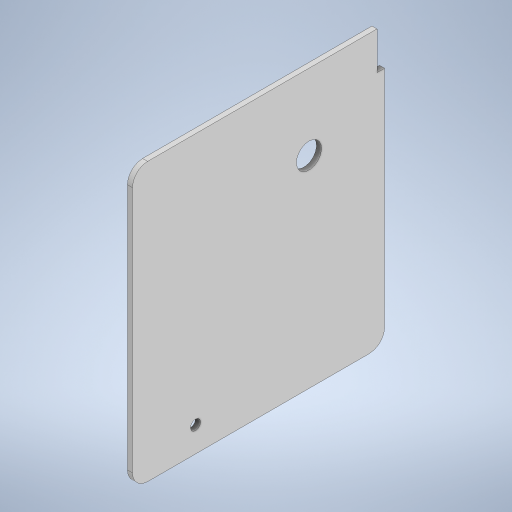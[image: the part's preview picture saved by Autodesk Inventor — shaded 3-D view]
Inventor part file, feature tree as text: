
AUTODESK INVENTOR PART (.ipt)
format: ipt  version: 2024.3 (Build 283343000, 343)  size: 229,376 bytes
history: native  units: mm
features: sheet_metal_op x1, chamfer x1, sketch x1, other x1
ambient origin geometry x8: Origin, YZ Plane, XZ Plane, XY Plane, X Axis, Y Axis, Z Axis, Center Point
bodies: Body1 (feature_tree)
feature tree (4):
  sheet_metal_op  "Face2"
  chamfer  "Corner Round2"
  sketch  "Sketch1"  dims[d0=110.0mm d1=100.0mm d2=3.0mm d3=15.0mm d4=4.0mm d5=10.0mm d6=25.0mm d9=10.0mm d10=30.0mm d11=30.0mm d12=2.0mm d13=6.0mm]
  other  "Plate2"
